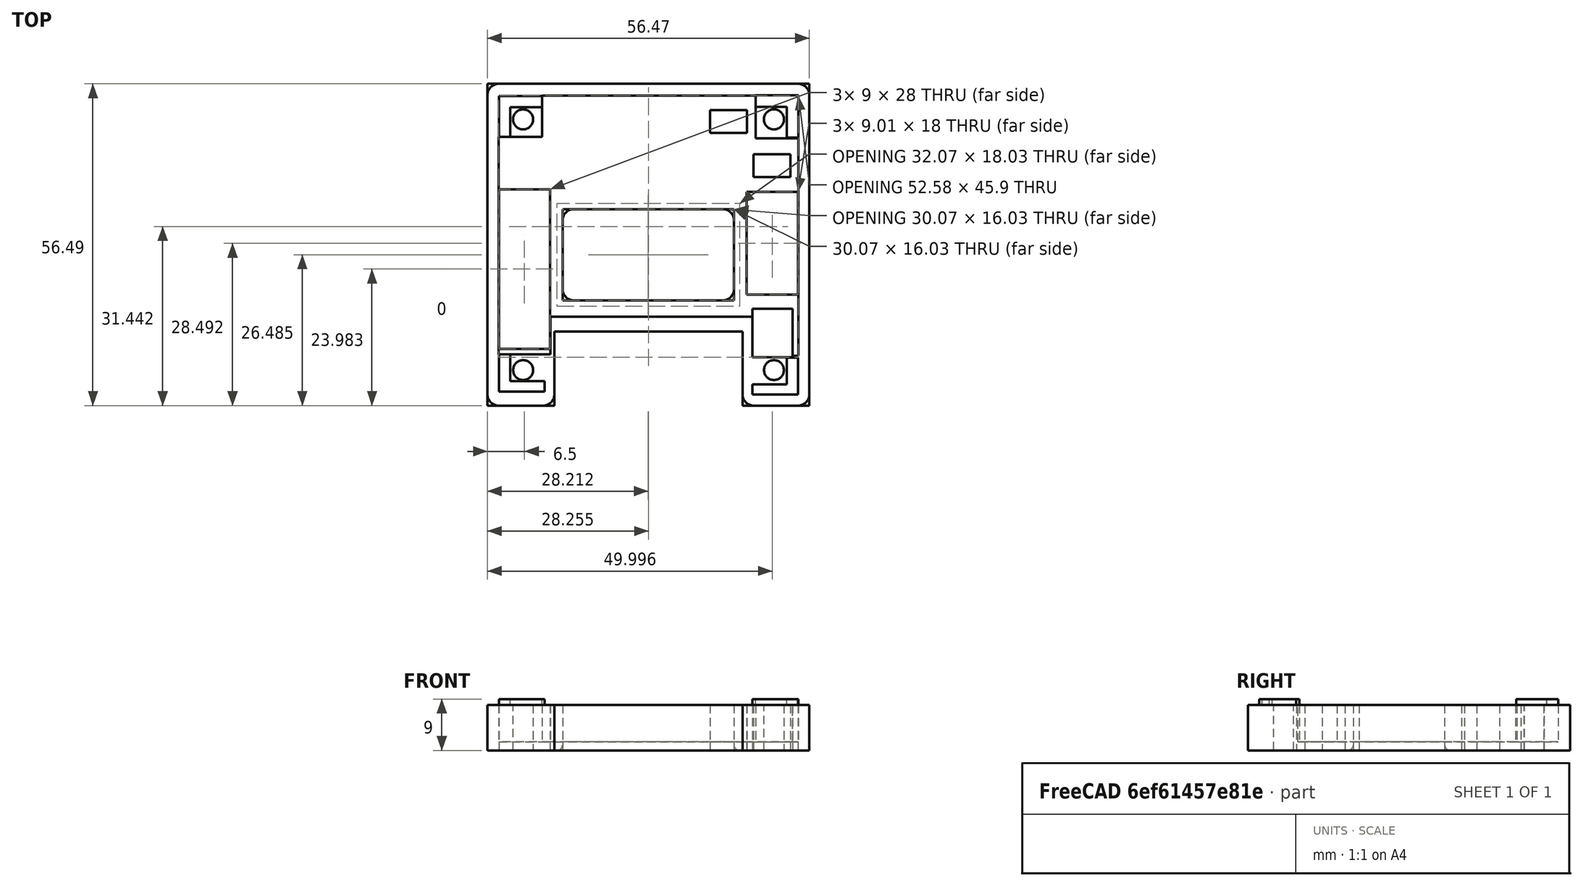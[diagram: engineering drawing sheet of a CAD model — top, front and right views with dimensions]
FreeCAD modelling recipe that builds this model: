
FCSTD DOCUMENT  (FreeCAD 0.16R6703 (Git))
Label: KK2.1-Case
License: FreeArt
LicenseURL: http://artlibre.org/licence/lal
objects: PartDesign::Fillet×4, Sketcher::SketchObject×3, PartDesign::Pad×2, Mesh::Feature×1, PartDesign::Pocket×1
note: 13 computed .brp shape members not serialized (recipe doc carries the construction recipe); baked Part::Feature solids carry a one-line shape summary decoded from their .brp

FEATURE [Mesh::Feature] KK2_CASE_TOP
  Placement = pos=(0,0,-33.5) rot=(0,0,1;0rad)
FEATURE [Sketcher::SketchObject] Sketch
  sketch-geometry (36):
    g0: LineSegment StartX=0 StartY=-23.7418 StartZ=0 EndX=11.7408 EndY=-23.7418 EndZ=0
    g1: LineSegment StartX=11.7408 StartY=-23.7418 StartZ=0 EndX=11.7408 EndY=-10.7418 EndZ=0
    g2: LineSegment StartX=11.7408 StartY=-10.7418 StartZ=0 EndX=44.7307 EndY=-10.7418 EndZ=0
    g3: LineSegment StartX=44.7307 StartY=-10.7418 StartZ=0 EndX=44.7307 EndY=-23.7418 EndZ=0
    g4: LineSegment StartX=44.7307 StartY=-23.7418 StartZ=0 EndX=56.4715 EndY=-23.7418 EndZ=0
    g5: LineSegment StartX=56.4715 StartY=-23.7418 StartZ=0 EndX=56.4715 EndY=32.7521 EndZ=0
    g6: LineSegment StartX=56.4715 StartY=32.7521 StartZ=0 EndX=0 EndY=32.7521 EndZ=0
    g7: LineSegment StartX=0 StartY=32.7521 StartZ=0 EndX=0 EndY=-23.7418 EndZ=0
    g8: LineSegment StartX=46.5 StartY=-15.2473 StartZ=0 EndX=53.4952 EndY=-15.2473 EndZ=0
    g9: LineSegment StartX=53.4952 StartY=-15.2473 StartZ=0 EndX=53.4952 EndY=-6.72671 EndZ=0
    g10: LineSegment StartX=53.4952 StartY=-6.72671 StartZ=0 EndX=46.5 EndY=-6.72671 EndZ=0
    g11: LineSegment StartX=46.5 StartY=-6.72671 StartZ=0 EndX=46.5 EndY=-15.2473 EndZ=0
    g12: Circle CenterX=50.2545 CenterY=-17.5 CenterZ=0 NormalX=0 NormalY=0 NormalZ=1 Radius=1.73974
    g13: Circle CenterX=6.264 CenterY=-17.5 CenterZ=0 NormalX=0 NormalY=0 NormalZ=1 Radius=1.74749
    g14: LineSegment StartX=2 StartY=14.2428 StartZ=0 EndX=11 EndY=14.2428 EndZ=0
    g15: LineSegment StartX=11 StartY=14.2428 StartZ=0 EndX=11 EndY=-13.7572 EndZ=0
    g16: LineSegment StartX=11 StartY=-13.7572 StartZ=0 EndX=2 EndY=-13.7572 EndZ=0
    g17: LineSegment StartX=2 StartY=-13.7572 StartZ=0 EndX=2 EndY=14.2428 EndZ=0
    g18: Circle CenterX=6.24896 CenterY=26.5 CenterZ=0 NormalX=0 NormalY=0 NormalZ=1 Radius=1.75633
    g19: Circle CenterX=50.249 CenterY=26.5 CenterZ=0 NormalX=0 NormalY=0 NormalZ=1 Radius=1.76734
    g20: LineSegment StartX=13.1758 StartY=10.7574 StartZ=0 EndX=43.2486 EndY=10.7574 EndZ=0
    g21: LineSegment StartX=43.2486 StartY=10.7574 StartZ=0 EndX=43.2486 EndY=-5.2681 EndZ=0
    g22: LineSegment StartX=43.2486 StartY=-5.2681 StartZ=0 EndX=13.1758 EndY=-5.2681 EndZ=0
    g23: LineSegment StartX=13.1758 StartY=-5.2681 StartZ=0 EndX=13.1758 EndY=10.7574 EndZ=0
    g24: LineSegment StartX=45.4913 StartY=13.7521 StartZ=0 EndX=54.5 EndY=13.7521 EndZ=0
    g25: LineSegment StartX=54.5 StartY=13.7521 StartZ=0 EndX=54.5 EndY=-4.2479 EndZ=0
    g26: LineSegment StartX=54.5 StartY=-4.2479 StartZ=0 EndX=45.4913 EndY=-4.2479 EndZ=0
    g27: LineSegment StartX=45.4913 StartY=-4.2479 StartZ=0 EndX=45.4913 EndY=13.7521 EndZ=0
    g28: LineSegment StartX=39.049 StartY=28.1381 StartZ=0 EndX=45.549 EndY=28.1381 EndZ=0
    g29: LineSegment StartX=45.549 StartY=28.1381 StartZ=0 EndX=45.549 EndY=24.149 EndZ=0
    g30: LineSegment StartX=45.549 StartY=24.149 StartZ=0 EndX=39.049 EndY=24.149 EndZ=0
    g31: LineSegment StartX=39.049 StartY=24.149 StartZ=0 EndX=39.049 EndY=28.1381 EndZ=0
    g32: LineSegment StartX=46.6569 StartY=20.4 StartZ=0 EndX=53.1569 EndY=20.4 EndZ=0
    g33: LineSegment StartX=53.1569 StartY=20.4 StartZ=0 EndX=53.1569 EndY=16.3951 EndZ=0
    g34: LineSegment StartX=53.1569 StartY=16.3951 StartZ=0 EndX=46.6569 EndY=16.3951 EndZ=0
    g35: LineSegment StartX=46.6569 StartY=16.3951 StartZ=0 EndX=46.6569 EndY=20.4 EndZ=0
  constraints (122):
    c: Horizontal(g0)
    c: Coincident(g0,g1)
    c: Vertical(g1)
    c: Coincident(g1,g2)
    c: Horizontal(g2)
    c: Coincident(g2,g3)
    c: Vertical(g3)
    c: Coincident(g3,g4)
    c: Horizontal(g4)
    c: Coincident(g4,g5)
    c: Vertical(g5)
    c: Coincident(g5,g6)
    c: Horizontal(g6)
    c: Coincident(g6,g7)
    c: Vertical(g7)
    c: Coincident(g7,g0)
    c: DistanceX(g0,g0) = 11.7408
    c: DistanceY(g0,g-1) = 23.7418
    c: DistanceX(g6,g6) = 56.4715
    c: DistanceY(g1,g1) = 13
    c: Equal(g1,g3)
    c: Equal(g0,g4)
    c: Equal(g7,g5)
    c: PointOnObject(g-1,g7)
    c: Coincident(g8,g9)
    c: Coincident(g9,g10)
    c: Coincident(g10,g11)
    c: Coincident(g11,g8)
    c: Horizontal(g8)
    c: Horizontal(g10)
    c: Vertical(g9)
    c: Vertical(g11)
    c: Equal(g11,g9)
    c: Equal(g10,g8)
    c: DistanceX(g10,g10) = 6.99516
    c: DistanceY(g11,g11) = 8.5206
    c: Distance(g4,g9) = 2.97634
    c: Distance(g4,g8) = 8.49449
    c: Distance(g12,g4) = 8.80969
    c: Radius(g12) = 1.73974
    c: Distance(g12,g3) = 8.33505
    c: Radius(g13) = 1.74749
    c: Distance(g13,g0) = 8.84295
    c: Distance(g13,g0) = 8.30394
    c: Coincident(g14,g15)
    c: Coincident(g15,g16)
    c: Coincident(g16,g17)
    c: Coincident(g17,g14)
    c: Horizontal(g14)
    c: Horizontal(g16)
    c: Vertical(g15)
    c: Vertical(g17)
    c: Equal(g16,g14)
    c: Equal(g17,g15)
    c: DistanceX(g14,g14) = 9
    c: DistanceY(g17,g17) = 28
    c: Distance(g0,g17) = 2
    c: Distance(g0,g16) = 9.98459
    c: Radius(g18) = 1.75633
    c: DistanceY(g7,g7) = 56.4939
    c: Distance(g18,g6) = 8.83956
    c: Distance(g18,g5) = 50.6102
    c: Radius(g19) = 1.76734
    c: Distance(g19,g5) = 8.82085
    c: Distance(g19,g6) = 50.6365
    c: Coincident(g20,g21)
    c: Coincident(g21,g22)
    c: Coincident(g22,g23)
    c: Coincident(g23,g20)
    c: Horizontal(g20)
    c: Horizontal(g22)
    c: Vertical(g21)
    c: Vertical(g23)
    c: Equal(g22,g20)
    c: DistanceY(g23,g23) = 16.0255
    c: DistanceX(g20,g20) = 30.0728
    c: Distance(g0,g23) = 13.1758
    c: Distance(g0,g22) = 18.4737
    c: Coincident(g24,g25)
    c: Coincident(g25,g26)
    c: Coincident(g26,g27)
    c: Coincident(g27,g24)
    c: Horizontal(g24)
    c: Horizontal(g26)
    c: Vertical(g25)
    c: Vertical(g27)
    c: Equal(g26,g24)
    c: Equal(g27,g25)
    c: DistanceX(g24,g24) = 9.00866
    c: Distance(g5,g25) = 1.9715
    c: Coincident(g28,g29)
    c: Coincident(g29,g30)
    c: Coincident(g30,g31)
    c: Coincident(g31,g28)
    c: Horizontal(g28)
    c: Horizontal(g30)
    c: Vertical(g29)
    c: Vertical(g31)
    c: Equal(g28,g30)
    c: Equal(g31,g29)
    c: DistanceY(g31,g31) = 3.98917
    c: DistanceX(g28,g28) = 6.5
    c: Distance(g19,g29) = 4.7
    c: Distance(g19,g28) = 1.63812
    c: Equal(g30,g28)
    c: Equal(g31,g29)
    c: Coincident(g32,g33)
    c: Coincident(g33,g34)
    c: Coincident(g34,g35)
    c: Coincident(g35,g32)
    c: Horizontal(g32)
    c: Horizontal(g34)
    c: Vertical(g33)
    c: Vertical(g35)
    c: Equal(g35,g33)
    c: Equal(g32,g34)
    c: DistanceY(g35,g35) = 4.00488
    c: DistanceX(g32,g32) = 6.5
    c: Distance(g19,g32) = 6.1
    c: Distance(g32,g5) = 3.31457
    c: DistanceY(g27,g27) = 18
    c: Distance(g5,g24) = 19
FEATURE [PartDesign::Pad] Pad
  Length = 8
  Length2 = 100
  Reversed = true
  Sketch = -> Sketch
  Type = 0
FEATURE [Sketcher::SketchObject] Sketch001
  Support = -> Pad [Face37]
  sketch-geometry (12):
    g0: LineSegment StartX=1.96636 StartY=23.4217 StartZ=0 EndX=9.59613 EndY=23.4217 EndZ=0
    g1: LineSegment StartX=9.59613 StartY=23.4217 StartZ=0 EndX=9.59613 EndY=30.6517 EndZ=0
    g2: LineSegment StartX=9.59613 StartY=30.6517 StartZ=0 EndX=47.0375 EndY=30.6517 EndZ=0
    g3: LineSegment StartX=47.0375 StartY=30.6517 StartZ=0 EndX=47.0375 EndY=23.1927 EndZ=0
    g4: LineSegment StartX=47.0375 StartY=23.1927 StartZ=0 EndX=54.5435 EndY=23.1927 EndZ=0
    g5: LineSegment StartX=54.5435 StartY=23.1927 StartZ=0 EndX=54.5435 EndY=-14.9592 EndZ=0
    g6: LineSegment StartX=54.5435 StartY=-14.9592 StartZ=0 EndX=46.5296 EndY=-14.9592 EndZ=0
    g7: LineSegment StartX=46.5296 StartY=-14.9592 StartZ=0 EndX=46.5296 EndY=-8.10114 EndZ=0
    g8: LineSegment StartX=46.5296 StartY=-8.10114 StartZ=0 EndX=11.0233 EndY=-8.10114 EndZ=0
    g9: LineSegment StartX=11.0233 StartY=-8.10114 StartZ=0 EndX=11.0233 EndY=-14.7302 EndZ=0
    g10: LineSegment StartX=11.0233 StartY=-14.7302 StartZ=0 EndX=1.96636 EndY=-14.7302 EndZ=0
    g11: LineSegment StartX=1.96636 StartY=-14.7302 StartZ=0 EndX=1.96636 EndY=23.4217 EndZ=0
  constraints (36):
    c: Horizontal(g0)
    c: Coincident(g0,g1)
    c: Vertical(g1)
    c: Coincident(g1,g2)
    c: Horizontal(g2)
    c: Coincident(g2,g3)
    c: Vertical(g3)
    c: Coincident(g3,g4)
    c: Horizontal(g4)
    c: Coincident(g4,g5)
    c: Vertical(g5)
    c: Coincident(g5,g6)
    c: Horizontal(g6)
    c: Coincident(g6,g7)
    c: Vertical(g7)
    c: Coincident(g7,g8)
    c: Horizontal(g8)
    c: Coincident(g8,g9)
    c: Vertical(g9)
    c: Coincident(g9,g10)
    c: Horizontal(g10)
    c: Coincident(g10,g11)
    c: Vertical(g11)
    c: Coincident(g0,g11)
    c: Equal(g11,g5)
    c: Distance(g-1,g11) = 1.96636
    c: Distance(g-1,g5) = 54.5435
    c: Distance(g-1,g0) = 23.5041
    c: Distance(g-1,g0) = 25.3113
    c: Distance(g-1,g1) = 32.1187
    c: Distance(g-1,g2) = 56.1431
    c: Distance(g-1,g3) = 52.4445
    c: Distance(g-1,g10) = 14.8609
    c: Distance(g-1,g9) = 18.3982
    c: Distance(g-1,g8) = 13.68
    c: Distance(g-1,g7) = 47.2296
FEATURE [PartDesign::Pocket] Pocket
  Length = 6.5
  Sketch = -> Sketch001
  Type = 0
FEATURE [PartDesign::Fillet] Fillet
  Base = -> Pocket [Edge69,Edge70,Edge2,Edge1]
  Radius = 2
FEATURE [PartDesign::Fillet] Fillet001
  Base = -> Fillet [Edge75,Edge77]
  Radius = 2
FEATURE [PartDesign::Fillet] Fillet002
  Base = -> Fillet001 [Edge144,Edge145,Edge143,Edge146]
  Radius = 2
FEATURE [PartDesign::Fillet] Fillet003
  Base = -> Fillet002 [Edge8,Edge7,Edge6,Edge4,Edge2,Edge1,Edge3,Edge5]
  Radius = 1
FEATURE [Sketcher::SketchObject] Sketch002
  Support = -> Fillet003 [Face56]
  sketch-geometry (24):
    g0: LineSegment StartX=2 StartY=-14.7539 StartZ=0 EndX=2 EndY=-21.2539 EndZ=0
    g1: LineSegment StartX=2 StartY=-21.2539 StartZ=0 EndX=10 EndY=-21.2539 EndZ=0
    g2: LineSegment StartX=10 StartY=-21.2539 StartZ=0 EndX=10 EndY=-19.4539 EndZ=0
    g3: LineSegment StartX=10 StartY=-19.4539 StartZ=0 EndX=4 EndY=-19.4539 EndZ=0
    g4: LineSegment StartX=4 StartY=-19.4539 StartZ=0 EndX=4 EndY=-14.7539 EndZ=0
    g5: LineSegment StartX=4 StartY=-14.7539 StartZ=0 EndX=2 EndY=-14.7539 EndZ=0
    g6: LineSegment StartX=54.5 StartY=-15.2962 StartZ=0 EndX=54.5 EndY=-21.7962 EndZ=0
    g7: LineSegment StartX=54.5 StartY=-21.7962 StartZ=0 EndX=46.5 EndY=-21.7962 EndZ=0
    g8: LineSegment StartX=46.5 StartY=-21.7962 StartZ=0 EndX=46.5 EndY=-19.9962 EndZ=0
    g9: LineSegment StartX=46.5 StartY=-19.9962 StartZ=0 EndX=52.5 EndY=-19.9962 EndZ=0
    g10: LineSegment StartX=52.5 StartY=-19.9962 StartZ=0 EndX=52.5 EndY=-15.2962 EndZ=0
    g11: LineSegment StartX=52.5 StartY=-15.2962 StartZ=0 EndX=54.5 EndY=-15.2962 EndZ=0
    g12: LineSegment StartX=47.0483 StartY=30.7038 StartZ=0 EndX=54.5171 EndY=30.7038 EndZ=0
    g13: LineSegment StartX=54.5171 StartY=30.7038 StartZ=0 EndX=54.5171 EndY=23.3149 EndZ=0
    g14: LineSegment StartX=54.5171 StartY=23.3149 StartZ=0 EndX=52.5171 EndY=23.3149 EndZ=0
    g15: LineSegment StartX=52.5171 StartY=23.3149 StartZ=0 EndX=52.5171 EndY=28.7038 EndZ=0
    g16: LineSegment StartX=52.5171 StartY=28.7038 StartZ=0 EndX=47.0483 EndY=28.7038 EndZ=0
    g17: LineSegment StartX=47.0483 StartY=28.7038 StartZ=0 EndX=47.0483 EndY=30.7038 EndZ=0
    g18: LineSegment StartX=2.0171 StartY=23.4021 StartZ=0 EndX=2.0171 EndY=30.6225 EndZ=0
    g19: LineSegment StartX=2.0171 StartY=30.6225 StartZ=0 EndX=9.59956 EndY=30.6225 EndZ=0
    g20: LineSegment StartX=9.59956 StartY=30.6225 StartZ=0 EndX=9.59956 EndY=28.6225 EndZ=0
    g21: LineSegment StartX=9.59956 StartY=28.6225 StartZ=0 EndX=4.0171 EndY=28.6225 EndZ=0
    g22: LineSegment StartX=4.0171 StartY=28.6225 StartZ=0 EndX=4.0171 EndY=23.4021 EndZ=0
    g23: LineSegment StartX=4.0171 StartY=23.4021 StartZ=0 EndX=2.0171 EndY=23.4021 EndZ=0
  constraints (72):
    c: Vertical(g0)
    c: Coincident(g0,g1)
    c: Horizontal(g1)
    c: Coincident(g1,g2)
    c: Vertical(g2)
    c: Coincident(g2,g3)
    c: Horizontal(g3)
    c: Coincident(g3,g4)
    c: Vertical(g4)
    c: Coincident(g4,g5)
    c: Coincident(g5,g0)
    c: DistanceY(g0,g0) = 6.5
    c: Horizontal(g5)
    c: DistanceX(g1,g1) = 8
    c: DistanceY(g2,g2) = 1.8
    c: Distance(g-1,g0) = 2
    c: DistanceX(g5,g5) = 2
    c: Distance(g-1,g1) = 21.2539
    c: Vertical(g6)
    c: Coincident(g6,g7)
    c: Horizontal(g7)
    c: Coincident(g7,g8)
    c: Vertical(g8)
    c: Coincident(g8,g9)
    c: Horizontal(g9)
    c: Coincident(g9,g10)
    c: Vertical(g10)
    c: Coincident(g10,g11)
    c: DistanceY(g8,g8) = 1.8
    c: Horizontal(g11)
    c: Coincident(g11,g6)
    c: DistanceY(g6,g6) = 6.5
    c: DistanceX(g11,g11) = 2
    c: DistanceX(g7,g7) = 8
    c: Distance(g0,g6) = 52.5
    c: Horizontal(g12)
    c: Coincident(g12,g13)
    c: Vertical(g13)
    c: Coincident(g13,g14)
    c: Horizontal(g14)
    c: Coincident(g14,g15)
    c: Vertical(g15)
    c: Coincident(g15,g16)
    c: Horizontal(g16)
    c: Coincident(g16,g17)
    c: Coincident(g17,g12)
    c: Vertical(g17)
    c: DistanceX(g14,g14) = 2
    c: DistanceY(g17,g17) = 2
    c: DistanceX(g12,g12) = 7.46875
    c: DistanceY(g13,g13) = 7.38888
    c: Distance(g12,g7) = 52.5
    c: Distance(g-1,g16) = 55.1131
    c: Distance(g-1,g15) = 52.5171
    c: Vertical(g18)
    c: Coincident(g18,g19)
    c: Horizontal(g19)
    c: Coincident(g19,g20)
    c: Vertical(g20)
    c: Coincident(g20,g21)
    c: Horizontal(g21)
    c: Coincident(g21,g22)
    c: Vertical(g22)
    c: Coincident(g22,g23)
    c: Horizontal(g23)
    c: Coincident(g18,g23)
    c: DistanceY(g20,g20) = 2
    c: DistanceX(g23,g23) = 2
    c: Distance(g12,g18) = 52.5
    c: DistanceX(g19,g19) = 7.58246
    c: DistanceY(g18,g18) = 7.22041
    c: Distance(g-1,g21) = 28.903
FEATURE [PartDesign::Pad] Pad001
  Length = 1
  Length2 = 100
  Sketch = -> Sketch002
  Type = 0
